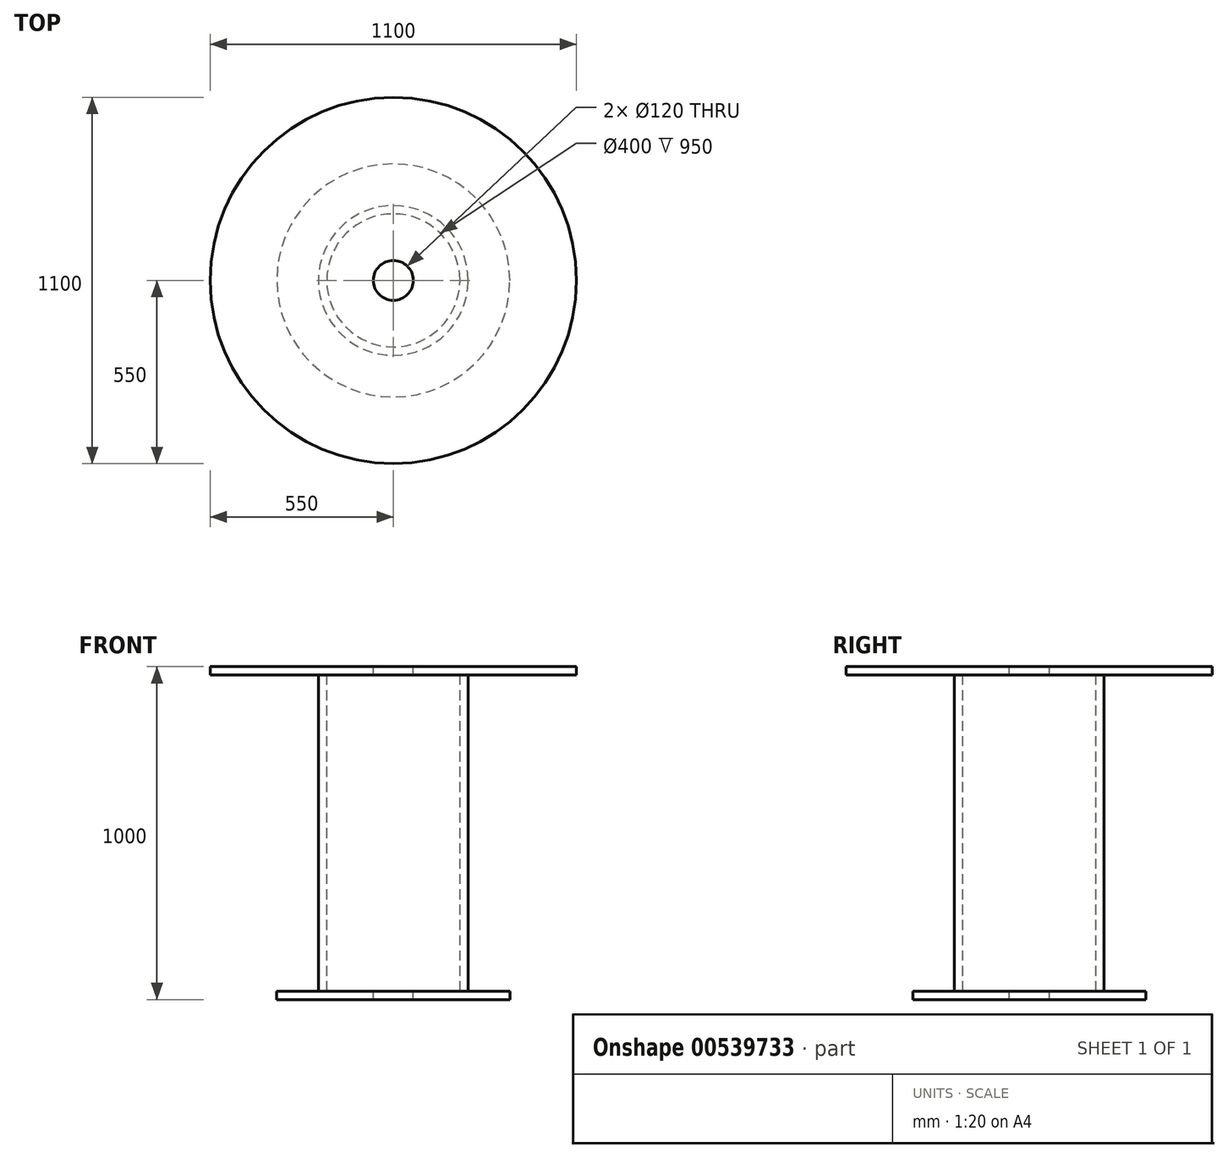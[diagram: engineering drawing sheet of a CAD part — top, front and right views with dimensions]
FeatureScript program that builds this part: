
annotation { "Feature Type Name" : "Feature", "Feature Type Description" : "" }
export const myFeature = defineFeature(function(context is Context, id is Id, definition is map)
    precondition{}
    {
        {
            var Q0;
            Q0=qCreatedBy(makeId("Top.planeOp"),FACE);
            var sketch = newSketch(context, id + "F0", { "sketchPlane" : qUnion([Q0])});
            skCircle(sketch, "E0", {"center": v(0, 0) * mm, "radius": 550 * mm});
            skCircle(sketch, "E1", {"center": v(0, 0) * mm, "radius": 60 * mm});
            skSolve(sketch);
        }
        {
            var Q0;
            Q0 = qSketchRegion(id + "F0", true);
            extrude(context, id + "F1", {"entities" : qUnion([Q0]), "oppositeDirection" : true, "depth" : 25 * mm, "offsetDistance" : 25 * mm});
        }
        {
            var Q0;
            Q0=makeQuery(id+"F1.opExtrude","CAP_FACE",FACE,{"disambiguationData":[OSD([sQuery(id+"F0.wireOp",EDGE,"E0"),sQuery(id+"F0.wireOp",EDGE,"E1")])],"isStart":false});
            var sketch = newSketch(context, id + "F2", { "sketchPlane" : qUnion([Q0])});
            skCircle(sketch, "E2", {"center": v(0, 0) * mm, "radius": 225 * mm});
            skCircle(sketch, "E3.0", {"center": v(0, 0) * mm, "radius": 200 * mm});
            skSolve(sketch);
        }
        {
            var Q0;
            Q0=makeQuery(id+"F2.imprint","IMPRINT",FACE,{"disambiguationData":[TD([[makeQuery(id+"F2.imprint","IMPRINT",EDGE,{"derivedFrom":sQuery(id+"F2.wireOp",EDGE,"E2")}),1.0]])]});
            extrude(context, id + "F3", {"entities" : qUnion([Q0]), "operationType" : NewBodyOperationType.ADD, "depth" : 950 * mm, "offsetDistance" : 25 * mm});
        }
        {
            var Q0;
            Q0=makeQuery(id+"F3.opExtrude","CAP_FACE",FACE,{"disambiguationData":[OSD([sQuery(id+"F2.wireOp",EDGE,"E2"),sQuery(id+"F2.wireOp",EDGE,"E3.0")])],"isStart":false});
            var sketch = newSketch(context, id + "F4", { "sketchPlane" : qUnion([Q0])});
            skCircle(sketch, "E4", {"center": v(0, 0) * mm, "radius": 350 * mm});
            skCircle(sketch, "E5", {"center": v(0, 0) * mm, "radius": 60 * mm});
            skSolve(sketch);
        }
        {
            var Q0;
            Q0=makeQuery(id+"F4.imprint","IMPRINT",FACE,{"disambiguationData":[TD([[makeQuery(id+"F4.imprint","IMPRINT",EDGE,{"derivedFrom":sQuery(id+"F4.wireOp",EDGE,"E4")}),1.0]])]});
            var Q1;
            Q1=makeQuery(id+"F4.imprint","IMPRINT",FACE,{"disambiguationData":[TD([[makeQuery(id+"F4.imprint","IMPRINT",EDGE,{"derivedFrom":sQuery(id+"F4.wireOp",EDGE,"E5")}),-1.0]])]});
            var Q2;
            Q2=makeQuery(id+"F4.imprint","IMPRINT",FACE,{"disambiguationData":[TD([[makeQuery(id+"F4.imprint","IMPRINT",EDGE,{"derivedFrom":makeQuery(id+"F3.opExtrude","CAP_EDGE",EDGE,{"disambiguationData":[OSD([sQuery(id+"F2.wireOp",EDGE,"E2")])],"isStart":false})}),1.0]])]});
            extrude(context, id + "F5", {"entities" : qUnion([Q0, Q1, Q2]), "operationType" : NewBodyOperationType.ADD, "depth" : 25 * mm, "offsetDistance" : 25 * mm});
        }
    });
